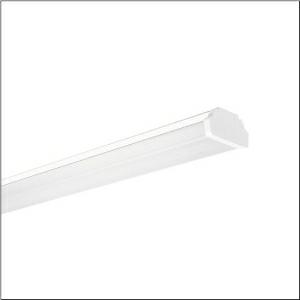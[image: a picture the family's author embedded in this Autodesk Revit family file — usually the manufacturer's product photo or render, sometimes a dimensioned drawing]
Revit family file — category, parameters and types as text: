
# Revit family: dus_r__31_ho_53bd812c1v4105_1de4
name_source: partatom
category: Lighting Fixtures
units: mm (PartAtom-declared; Revit-internal decimal feet)

## family parameters
Cut with Voids When Loaded = No
Host = Face
Light Source = No
Part Type = Normal
Room Calculation Point = No
Round Connector Dimension = Use Diameter
Shared = No

## types (1)
- --- (1 x LED, 10520 lm, 63.8 W, 4000K)
    Apparent Load = 64 VA
    CIE Flux Codes = 47 80 95 92 100
    Color Rendering = 80
    Color Temperature = 4000K
    Default Elevation = 1800 mm
    Description = DUS® 31 HO, luminaire insert, of sheet steel, coil coated, white, length: 1.535mm, width: 81mm, height: 90mm, 5x system unit, system units: 307mm, LED rated luminous flux: 10.520lm, light colour: 840, control gear: ON/OFF Multilumen, CLOi, control gear: ECG Multilumen, with plug, 3-pole, with phase selection, mains connection: 220..240V, AC, 50/60Hz, start of lifetime: 64W, end of service life: 73W, through-wiring accessed according to module size, primary optical cover: cover, of PMMA, light emission: direct distribution, primary light characteristic: symmetric, protection rating (complete): IP20, protection rating (LED compartment): IP50, insulation class (complete): insulation class I (protective earthing), certification: CE, ENEC, VDE, UKCA, impact resistance: IK03, permissible ambient temperature for indoor applications: -35..+35°C, corresponds to IFS (International Featured Standards) requirements for safety and quality in the food industry, reducing of maximum allowable ambient temperature of 5°C with ceiling mounting, packaging unit: 1 piece
    Height = 95 mm
    Lamp = 1 x LED
    Lamp Light Flux = 10520 lm
    Lamp Power = 63.8 W
    Lamp count = 1
    Length = 1535 mm
    Luminous efficacy = 165 lm/W
    Manufacturer = Siteco
    ModVariant = No
    Model = 53BD812C1V4105
    Mounting Place = Ceiling
    Mounting Type = Pendant
    Number of Poles = 1
    OnlyDefault = Yes
    Power Factor = 1
    Product Name = DUS® 31 HO
    Product group = luminaire insert | ceiling pendant
    ProductGroupID = 902
    Protection Class = Protection class I
    Protection Degree = IP 20
    RLX_Detail_Level = 1
    RLX_Emergency_Light_Flux = 0 lm
    RLX_Emergency_Type = 0
    RLX_Emergency_Type_DB = No
    RlxData = <blob elided: 40001 chars, md5=5dc71a65>
    Socket = socket
    Standby Power = 0 W
    System Light Flux = 10520 lm
    System Power = 64 W
    Type Comments = factory setting: luminous flux: 100 % | (A | C | E) | 144 mA
    Type Image = l_1319596.jpg
    URL = http://relux.com
    VarID = @adj_219505
    Voltage = 0 V
    Weight = 0.00 kg
    Width = 81 mm

## geometry (parser evidence)
native form markers: Blend x4, Sweep x12
no freeform markers — native parametric forms only
